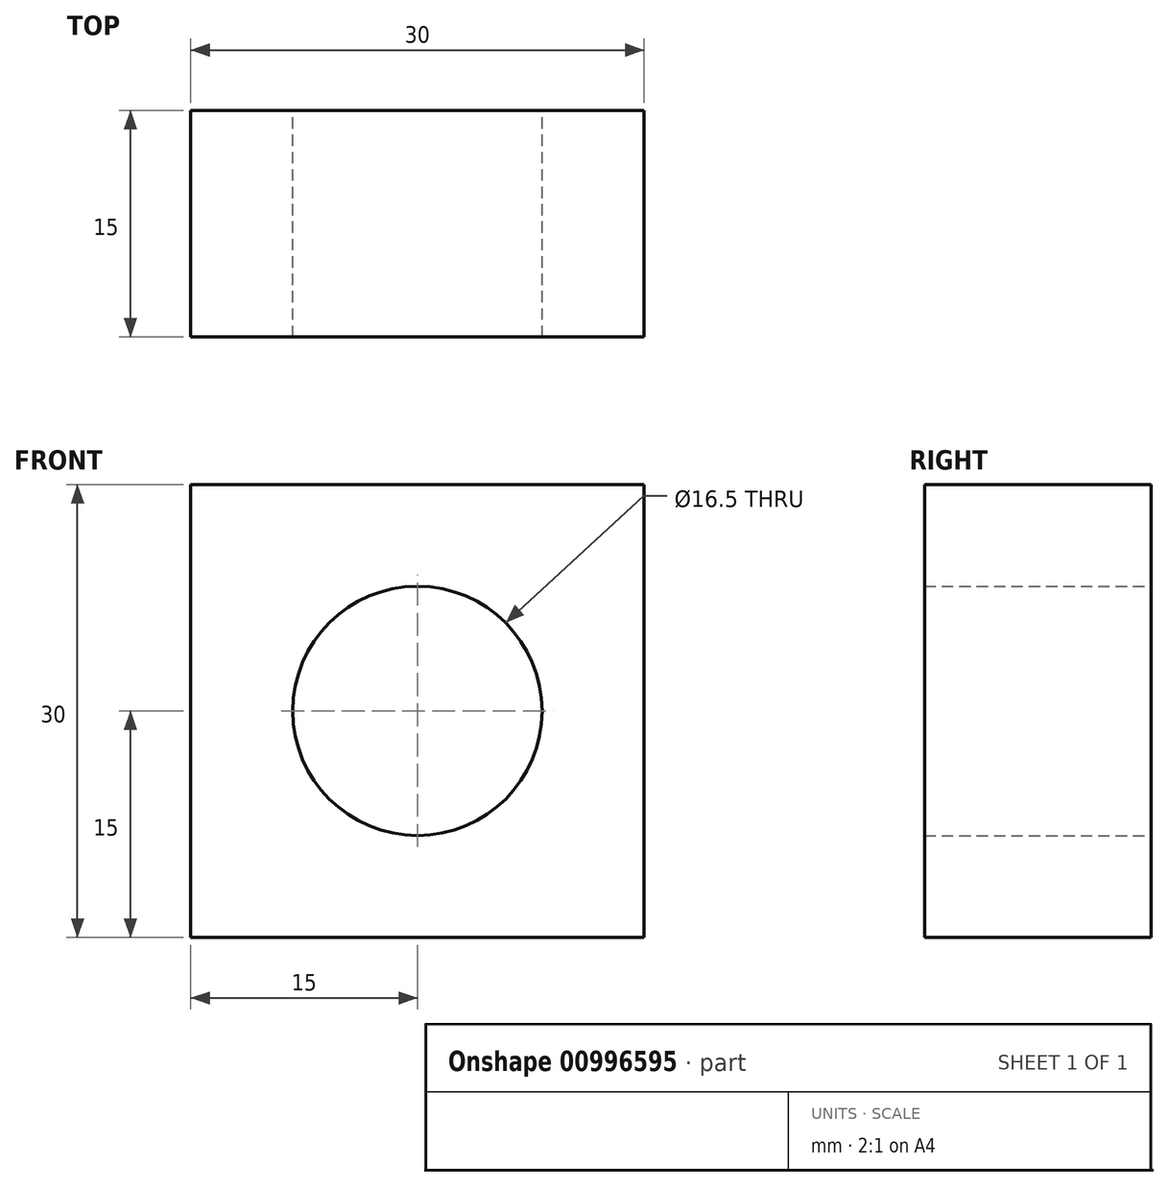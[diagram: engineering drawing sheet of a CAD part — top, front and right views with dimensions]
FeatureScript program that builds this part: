
annotation { "Feature Type Name" : "Feature", "Feature Type Description" : "" }
export const myFeature = defineFeature(function(context is Context, id is Id, definition is map)
    precondition{}
    {
        {
            var Q0;
            Q0=qCreatedBy(makeId("Front.planeOp"),FACE);
            var sketch = newSketch(context, id + "F0", { "sketchPlane" : qUnion([Q0])});
            skLineSegment(sketch, "E0.bottom", {"start": v(-15, 15) * mm, "end": v(15, 15) * mm});
            skLineSegment(sketch, "E0.top", {"start": v(-15, -15) * mm, "end": v(15, -15) * mm});
            skLineSegment(sketch, "E0.left", {"start": v(-15, 15) * mm, "end": v(-15, -15) * mm});
            skLineSegment(sketch, "E0.right", {"start": v(15, 15) * mm, "end": v(15, -15) * mm});
            skSolve(sketch);
        }
        {
            var Q0;
            Q0=makeQuery(id+"F0.imprint","IMPRINT",FACE,{"disambiguationData":[TD([[makeQuery(id+"F0.imprint","IMPRINT",EDGE,{"derivedFrom":sQuery(id+"F0.wireOp",EDGE,"E0.bottom")}),-1.0]])]});
            extrude(context, id + "F1", {"entities" : qUnion([Q0]), "depth" : 15 * mm, "offsetDistance" : 25 * mm});
        }
        {
            var Q0;
            Q0=makeQuery(id+"F1.opExtrude","CAP_FACE",FACE,{"disambiguationData":[OSD([sQuery(id+"F0.wireOp",EDGE,"E0.bottom"),sQuery(id+"F0.wireOp",EDGE,"E0.top"),sQuery(id+"F0.wireOp",EDGE,"E0.left"),sQuery(id+"F0.wireOp",EDGE,"E0.right")])],"isStart":true});
            var sketch = newSketch(context, id + "F2", { "sketchPlane" : qUnion([Q0])});
            skPoint(sketch, "E1", {"position": v(0, 0) * mm});
            skSolve(sketch);
        }
        {
            var Q0;
            Q0=sQuery(id+"F2.wireOp",VERTEX,"E1");
            var Q1;
            Q1=makeQuery(id+"F1.opExtrude","SWEPT_BODY",BODY,{"disambiguationData":[OSD([sQuery(id+"F0.wireOp",EDGE,"E0.bottom"),sQuery(id+"F0.wireOp",EDGE,"E0.top"),sQuery(id+"F0.wireOp",EDGE,"E0.left"),sQuery(id+"F0.wireOp",EDGE,"E0.right")])]});
            hole(context, id + "F3", {"style" : HoleStyle.SIMPLE, "endStyle" : HoleEndStyle.THROUGH, "standardTappedOrClearance" : lookupTablePath({ "standard" : "ISO", "engagement" : "75%", "pitch" : "1.5 mm", "size" : "M18", "type" : "Tapped" }), "standardBlindInLast" : lookupTablePath({ "standard" : "ISO", "fit" : "Normal", "engagement" : "75%", "pitch" : "1.5 mm", "size" : "M18", "type" : "Clearance & tapped" }), "holeDiameter" : 16.5 * mm, "majorDiameter" : 18 * mm, "showTappedDepth" : true, "isTappedThrough" : true, "tappedDepth" : 16 * mm, "tapClearance" : 3, "locations" : qUnion([Q0]), "scope" : qUnion([Q1])});
        }
    });
